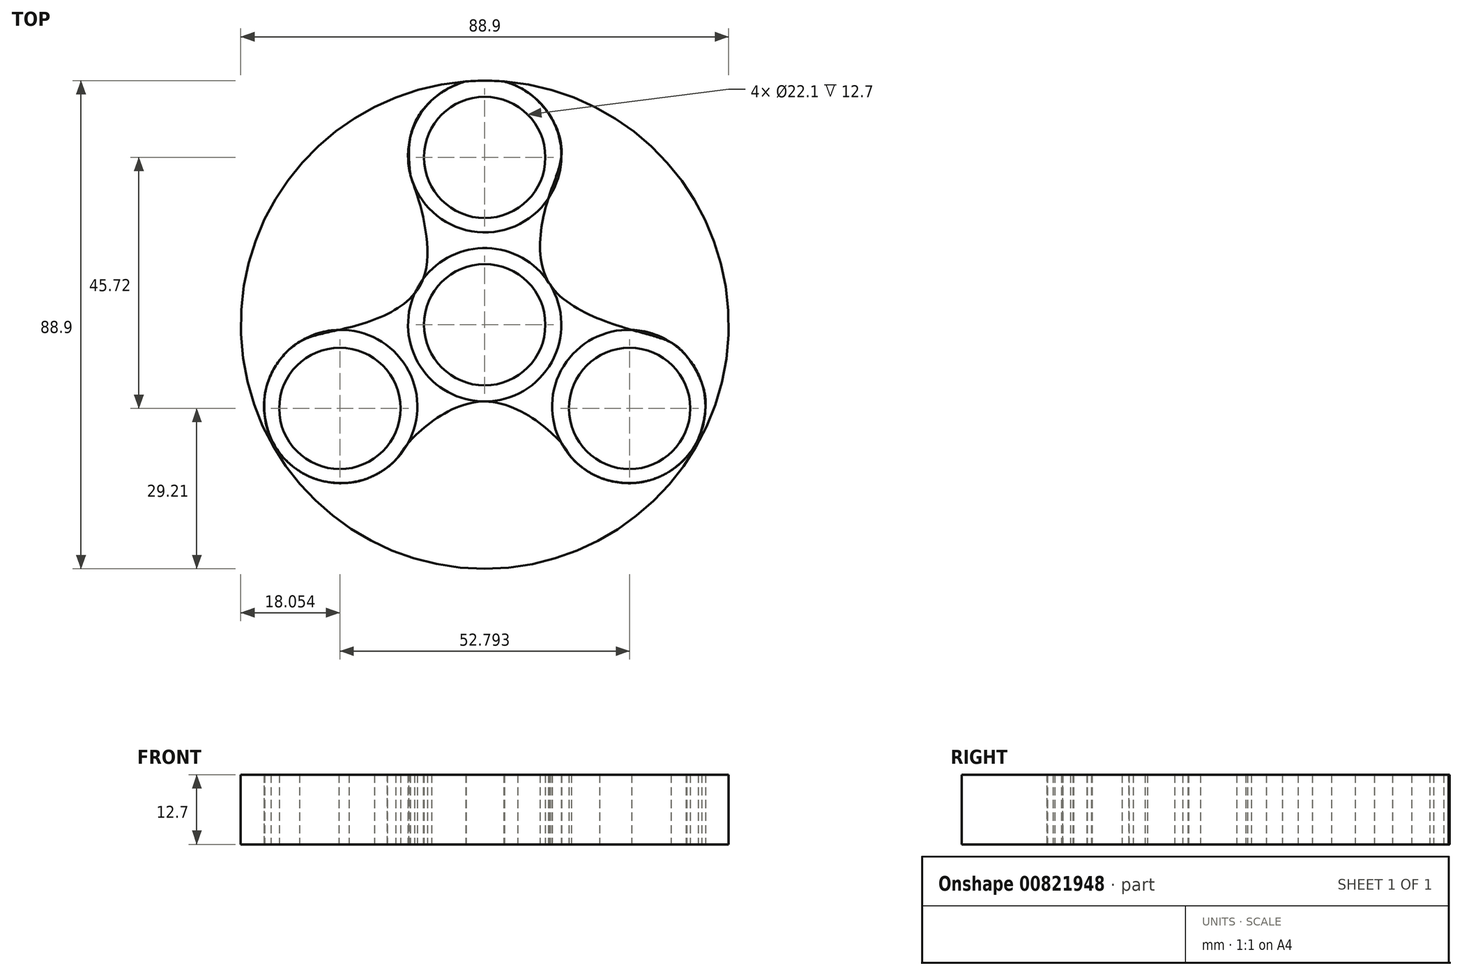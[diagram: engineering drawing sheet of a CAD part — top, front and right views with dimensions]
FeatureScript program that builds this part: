
annotation { "Feature Type Name" : "Feature", "Feature Type Description" : "" }
export const myFeature = defineFeature(function(context is Context, id is Id, definition is map)
    precondition{}
    {
        {
            var Q0;
            Q0=qCreatedBy(makeId("Top.planeOp"),FACE);
            var sketch = newSketch(context, id + "F0", { "sketchPlane" : qUnion([Q0])});
            skCircle(sketch, "E0", {"center": v(0, 0) * mm, "radius": 44.45 * mm});
            skCircle(sketch, "E1", {"center": v(0, 0) * mm, "radius": 11.05 * mm});
            skLineSegment(sketch, "E2", {"start": v(0, 0) * mm, "end": v(0, 30.48) * mm});
            skCircle(sketch, "E3", {"center": v(0, 30.48) * mm, "radius": 11.05 * mm});
            skCircle(sketch, "E4.1.0", {"center": v(-26.4, -15.24) * mm, "radius": 11.05 * mm});
            skCircle(sketch, "E4.2.0", {"center": v(26.4, -15.24) * mm, "radius": 11.05 * mm});
            skSolve(sketch);
        }
        {
            var Q0;
            Q0=makeQuery(id+"F0.imprint","IMPRINT",FACE,{"disambiguationData":[TD([[makeQuery(id+"F0.imprint","IMPRINT",EDGE,{"derivedFrom":sQuery(id+"F0.wireOp",EDGE,"E0")}),1.0]])]});
            var sketch = newSketch(context, id + "F1", { "sketchPlane" : qUnion([Q0])});
            skCircle(sketch, "E5", {"center": v(0, 0) * mm, "radius": 13.97 * mm});
            skCircle(sketch, "E6", {"center": v(0, 30.78) * mm, "radius": 13.97 * mm});
            skCircle(sketch, "E7", {"center": v(-26.24, -14.9) * mm, "radius": 13.97 * mm});
            skCircle(sketch, "E8", {"center": v(26.24, -14.9) * mm, "radius": 13.97 * mm});
            skFitSpline(sketch, "E9", {"points": [v(-26.55, -0.93) * mm, v(-11.2, 8.36) * mm, v(-13.22, 26.28) * mm, v(-13.52, 27.26) * mm, v(-13.58, 34.05) * mm, v(-9.67, 40.87) * mm, v(-2.32, 44.56) * mm, v(6.03, 43.39) * mm, v(12.23, 37.54) * mm, v(13.97, 30.78) * mm, v(11.58, 22.97) * mm, v(11.7, 7.65) * mm, v(26.79, -0.94) * mm, v(33.93, -3.23) * mm, v(36.68, -5.61) * mm, v(39.53, -10.57) * mm, v(40.21, -15.2) * mm, v(38.9, -20.8) * mm, v(36.78, -24.07) * mm, v(33.45, -26.86) * mm, v(27.4, -28.82) * mm, v(20.95, -27.82) * mm, v(17.77, -26) * mm, v(15.82, -24.2) * mm, v(13.98, -21.59) * mm, v(0, -13.97) * mm, v(-14, -21.6) * mm, v(-16.22, -24.63) * mm, v(-20.11, -27.45) * mm, v(-24.75, -28.79) * mm, v(-30.37, -28.24) * mm, v(-35.25, -25.58) * mm, v(-38.96, -20.68) * mm, v(-40.11, -13.2) * mm, v(-37.86, -7.14) * mm, v(-33.73, -3.1) * mm, v(-26.55, -0.93) * mm]});
            skSolve(sketch);
        }
        {
            var Q0;
            Q0=makeQuery(id+"F0.imprint","IMPRINT",FACE,{"disambiguationData":[TD([[makeQuery(id+"F0.imprint","IMPRINT",EDGE,{"derivedFrom":sQuery(id+"F0.wireOp",EDGE,"E4.1.0")}),1.0]])]});
            var Q1;
            Q1=makeQuery(id+"F0.imprint","IMPRINT",FACE,{"disambiguationData":[TD([[makeQuery(id+"F0.imprint","IMPRINT",EDGE,{"derivedFrom":sQuery(id+"F0.wireOp",EDGE,"E1")}),1.0]])]});
            var Q2;
            Q2=makeQuery(id+"F0.imprint","IMPRINT",FACE,{"disambiguationData":[TD([[makeQuery(id+"F0.imprint","IMPRINT",EDGE,{"derivedFrom":sQuery(id+"F0.wireOp",EDGE,"E3")}),1.0]])]});
            var Q3;
            Q3=makeQuery(id+"F0.imprint","IMPRINT",FACE,{"disambiguationData":[TD([[makeQuery(id+"F0.imprint","IMPRINT",EDGE,{"derivedFrom":sQuery(id+"F0.wireOp",EDGE,"E4.2.0")}),1.0]])]});
            extrude(context, id + "F2", {"entities" : qUnion([Q0, Q1, Q2, Q3]), "depth" : 12.7 * mm, "offsetDistance" : 25.4 * mm});
        }
        {
            var Q0;
            {var subQ0=sQuery(id+"F1.wireOp",EDGE,"E9");var subQ1=sQuery(id+"F1.wireOp",EDGE,"E5");var subQ2=makeQuery(id+"F1.imprint","INTERSECT",VERTEX,{"disambiguationData":[OD(2.0)],"derivedFrom":[subQ1,subQ0]});Q0=makeQuery(id+"F1.imprint","IMPRINT",FACE,{"disambiguationData":[TD([[makeQuery(id+"F1.imprint","IMPRINT",EDGE,{"disambiguationData":[TD([[subQ2,-1.0]])],"derivedFrom":subQ1}),-1.0]])]});}
            var Q1;
            {var subQ0=sQuery(id+"F1.wireOp",EDGE,"E9");var subQ1=sQuery(id+"F1.wireOp",EDGE,"E5");var subQ2=makeQuery(id+"F1.imprint","INTERSECT",VERTEX,{"disambiguationData":[OD(0.0)],"derivedFrom":[subQ1,subQ0]});Q1=makeQuery(id+"F1.imprint","IMPRINT",FACE,{"disambiguationData":[TD([[makeQuery(id+"F1.imprint","IMPRINT",EDGE,{"disambiguationData":[TD([[subQ2,1.0]])],"derivedFrom":subQ1}),-1.0]])]});}
            var Q2;
            {var subQ0=sQuery(id+"F1.wireOp",EDGE,"E9");var subQ1=sQuery(id+"F1.wireOp",EDGE,"E5");var subQ2=makeQuery(id+"F1.imprint","INTERSECT",VERTEX,{"disambiguationData":[OD(1.0)],"derivedFrom":[subQ1,subQ0]});Q2=makeQuery(id+"F1.imprint","IMPRINT",FACE,{"disambiguationData":[TD([[makeQuery(id+"F1.imprint","IMPRINT",EDGE,{"disambiguationData":[TD([[subQ2,-1.0]])],"derivedFrom":subQ1}),-1.0]])]});}
            var Q3;
            Q3=makeQuery(id+"F1.imprint","IMPRINT",FACE,{"disambiguationData":[TD([[makeQuery(id+"F1.imprint","IMPRINT",EDGE,{"derivedFrom":makeQuery(id+"F0.imprint","IMPRINT",EDGE,{"derivedFrom":sQuery(id+"F0.wireOp",EDGE,"E1")})}),-1.0]])]});
            var Q4;
            Q4=makeQuery(id+"F1.imprint","IMPRINT",FACE,{"disambiguationData":[TD([[makeQuery(id+"F1.imprint","IMPRINT",EDGE,{"derivedFrom":makeQuery(id+"F0.imprint","IMPRINT",EDGE,{"derivedFrom":sQuery(id+"F0.wireOp",EDGE,"E4.1.0")})}),-1.0]])]});
            var Q5;
            Q5=makeQuery(id+"F1.imprint","IMPRINT",FACE,{"disambiguationData":[TD([[makeQuery(id+"F1.imprint","IMPRINT",EDGE,{"derivedFrom":makeQuery(id+"F0.imprint","IMPRINT",EDGE,{"derivedFrom":sQuery(id+"F0.wireOp",EDGE,"E4.2.0")})}),-1.0]])]});
            var Q6;
            Q6=makeQuery(id+"F1.imprint","IMPRINT",FACE,{"disambiguationData":[TD([[makeQuery(id+"F1.imprint","IMPRINT",EDGE,{"derivedFrom":makeQuery(id+"F0.imprint","IMPRINT",EDGE,{"derivedFrom":sQuery(id+"F0.wireOp",EDGE,"E3")})}),-1.0]])]});
            extrude(context, id + "F3", {"entities" : qUnion([Q0, Q1, Q2, Q3, Q4, Q5, Q6]), "depth" : 12.7 * mm, "offsetDistance" : 25.4 * mm});
        }
        {
            var Q0;
            Q0=makeQuery(id+"F2.opExtrude","CAP_FACE",FACE,{"disambiguationData":[OSD([sQuery(id+"F0.wireOp",EDGE,"E4.1.0")])],"isStart":false});
            var Q1;
            Q1=makeQuery(id+"F2.opExtrude","CAP_FACE",FACE,{"disambiguationData":[OSD([sQuery(id+"F0.wireOp",EDGE,"E1")])],"isStart":false});
            var Q2;
            Q2=makeQuery(id+"F2.opExtrude","CAP_FACE",FACE,{"disambiguationData":[OSD([sQuery(id+"F0.wireOp",EDGE,"E3")])],"isStart":false});
            var Q3;
            Q3=makeQuery(id+"F2.opExtrude","CAP_FACE",FACE,{"disambiguationData":[OSD([sQuery(id+"F0.wireOp",EDGE,"E4.2.0")])],"isStart":false});
            extrude(context, id + "F4", {"entities" : qUnion([Q0, Q1, Q2, Q3]), "operationType" : NewBodyOperationType.REMOVE, "endBound" : BoundingType.THROUGH_ALL, "oppositeDirection" : true, "depth" : 25.4 * mm, "offsetDistance" : 25.4 * mm});
        }
    });
